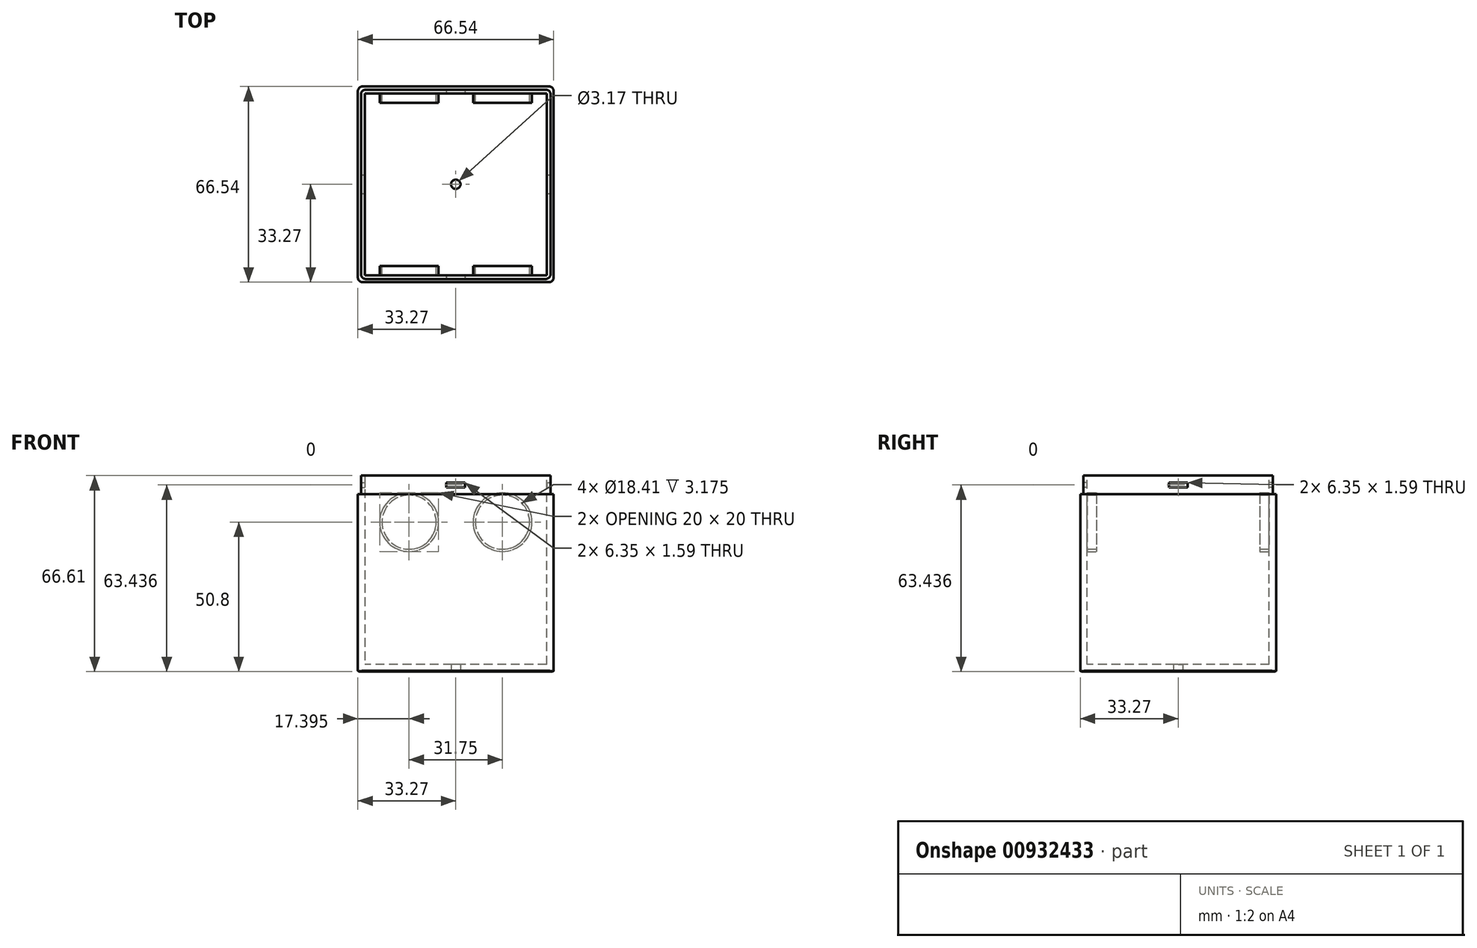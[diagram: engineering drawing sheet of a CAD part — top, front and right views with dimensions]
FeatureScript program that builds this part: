
annotation { "Feature Type Name" : "Feature", "Feature Type Description" : "" }
export const myFeature = defineFeature(function(context is Context, id is Id, definition is map)
    precondition{}
    {
        {
            var Q0;
            Q0=qCreatedBy(makeId("Top.planeOp"),FACE);
            var sketch = newSketch(context, id + "F0", { "sketchPlane" : qUnion([Q0])});
            skLineSegment(sketch, "E0.bottom", {"start": v(34.1, 34.1) * mm, "end": v(-34.1, 34.1) * mm});
            skLineSegment(sketch, "E0.top", {"start": v(34.1, -34.1) * mm, "end": v(-34.1, -34.1) * mm});
            skLineSegment(sketch, "E0.left", {"start": v(34.1, 34.1) * mm, "end": v(34.1, -34.1) * mm});
            skLineSegment(sketch, "E0.right", {"start": v(-34.1, 34.1) * mm, "end": v(-34.1, -34.1) * mm});
            skPoint(sketch, "E0.middle", {"position": v(0, 0) * mm});
            skSolve(sketch);
        }
        {
            var Q0;
            Q0 = qSketchRegion(id + "F0", true);
            extrude(context, id + "F1", {"entities" : qUnion([Q0]), "depth" : 66.61 * mm, "offsetDistance" : 25.4 * mm});
        }
        {
            var Q0;
            Q0=makeQuery(id+"F1.opExtrude","SWEPT_EDGE",EDGE,{"disambiguationData":[OSD([sQuery(id+"F0.wireOp",EDGE,"E0.bottom"),sQuery(id+"F0.wireOp",EDGE,"E0.right")])]});
            var Q1;
            Q1=makeQuery(id+"F1.opExtrude","CAP_EDGE",EDGE,{"disambiguationData":[OSD([sQuery(id+"F0.wireOp",EDGE,"E0.right")])],"isStart":true});
            var Q2;
            Q2=makeQuery(id+"F1.opExtrude","SWEPT_EDGE",EDGE,{"disambiguationData":[OSD([sQuery(id+"F0.wireOp",EDGE,"E0.top"),sQuery(id+"F0.wireOp",EDGE,"E0.right")])]});
            var Q3;
            Q3=makeQuery(id+"F1.opExtrude","SWEPT_EDGE",EDGE,{"disambiguationData":[OSD([sQuery(id+"F0.wireOp",EDGE,"E0.top"),sQuery(id+"F0.wireOp",EDGE,"E0.left")])]});
            var Q4;
            Q4=makeQuery(id+"F1.opExtrude","CAP_EDGE",EDGE,{"disambiguationData":[OSD([sQuery(id+"F0.wireOp",EDGE,"E0.top")])],"isStart":true});
            var Q5;
            Q5=makeQuery(id+"F1.opExtrude","CAP_FACE",FACE,{"disambiguationData":[OSD([sQuery(id+"F0.wireOp",EDGE,"E0.bottom"),sQuery(id+"F0.wireOp",EDGE,"E0.top"),sQuery(id+"F0.wireOp",EDGE,"E0.left"),sQuery(id+"F0.wireOp",EDGE,"E0.right")])],"isStart":true});
            var Q6;
            Q6=makeQuery(id+"F1.opExtrude","SWEPT_EDGE",EDGE,{"disambiguationData":[OSD([sQuery(id+"F0.wireOp",EDGE,"E0.bottom"),sQuery(id+"F0.wireOp",EDGE,"E0.left")])]});
            fillet(context, id + "F2", {"entities" : qUnion([Q0, Q1, Q2, Q3, Q4, Q5, Q6]), "radius" : 1.59 * mm, "tangentPropagation" : true, "allowEdgeOverflow" : false});
        }
        {
            var Q0;
            Q0=makeQuery(id+"F1.opExtrude","CAP_FACE",FACE,{"disambiguationData":[OSD([sQuery(id+"F0.wireOp",EDGE,"E0.bottom"),sQuery(id+"F0.wireOp",EDGE,"E0.top"),sQuery(id+"F0.wireOp",EDGE,"E0.left"),sQuery(id+"F0.wireOp",EDGE,"E0.right")])],"isStart":false});
            shell(context, id + "F3", {"entities" : qUnion([Q0]), "thickness" : 3.17 * mm});
        }
        {
            var Q0;
            Q0=makeQuery(id+"F3.opShell","OFFSET_FACE",FACE,{"disambiguationData":[OSD([sQuery(id+"F0.wireOp",EDGE,"E0.bottom"),sQuery(id+"F0.wireOp",EDGE,"E0.top"),sQuery(id+"F0.wireOp",EDGE,"E0.left"),sQuery(id+"F0.wireOp",EDGE,"E0.right")])]});
            var sketch = newSketch(context, id + "F4", { "sketchPlane" : qUnion([Q0])});
            skLineSegment(sketch, "E1.bottom", {"start": v(-30.92, 30.92) * mm, "end": v(-27.75, 30.92) * mm});
            skLineSegment(sketch, "E1.top", {"start": v(-30.92, 27.75) * mm, "end": v(-27.75, 27.75) * mm});
            skLineSegment(sketch, "E1.left", {"start": v(-30.92, 30.92) * mm, "end": v(-30.92, 27.75) * mm});
            skLineSegment(sketch, "E1.right", {"start": v(-27.75, 30.92) * mm, "end": v(-27.75, 27.75) * mm});
            skLineSegment(sketch, "E2.bottom", {"start": v(30.92, 30.92) * mm, "end": v(27.75, 30.92) * mm});
            skLineSegment(sketch, "E2.top", {"start": v(30.92, 27.75) * mm, "end": v(27.75, 27.75) * mm});
            skLineSegment(sketch, "E2.left", {"start": v(30.92, 30.92) * mm, "end": v(30.92, 27.75) * mm});
            skLineSegment(sketch, "E2.right", {"start": v(27.75, 30.92) * mm, "end": v(27.75, 27.75) * mm});
            skLineSegment(sketch, "E3.bottom", {"start": v(-30.92, -30.92) * mm, "end": v(-27.75, -30.92) * mm});
            skLineSegment(sketch, "E3.top", {"start": v(-30.92, -27.75) * mm, "end": v(-27.75, -27.75) * mm});
            skLineSegment(sketch, "E3.left", {"start": v(-30.92, -30.92) * mm, "end": v(-30.92, -27.75) * mm});
            skLineSegment(sketch, "E3.right", {"start": v(-27.75, -30.92) * mm, "end": v(-27.75, -27.75) * mm});
            skLineSegment(sketch, "E4.bottom", {"start": v(30.92, -30.92) * mm, "end": v(27.75, -30.92) * mm});
            skLineSegment(sketch, "E4.top", {"start": v(30.92, -27.75) * mm, "end": v(27.75, -27.75) * mm});
            skLineSegment(sketch, "E4.left", {"start": v(30.92, -30.92) * mm, "end": v(30.92, -27.75) * mm});
            skLineSegment(sketch, "E4.right", {"start": v(27.75, -30.92) * mm, "end": v(27.75, -27.75) * mm});
            skLineSegment(sketch, "E5.bottom", {"start": v(-3.18, 30.92) * mm, "end": v(3.17, 30.92) * mm});
            skLineSegment(sketch, "E5.top", {"start": v(-3.18, 27.75) * mm, "end": v(3.17, 27.75) * mm});
            skLineSegment(sketch, "E5.left", {"start": v(-3.18, 30.92) * mm, "end": v(-3.18, 27.75) * mm});
            skLineSegment(sketch, "E5.right", {"start": v(3.17, 30.92) * mm, "end": v(3.17, 27.75) * mm});
            skLineSegment(sketch, "E6.bottom", {"start": v(-30.92, 3.17) * mm, "end": v(-27.75, 3.17) * mm});
            skLineSegment(sketch, "E6.top", {"start": v(-30.92, -3.18) * mm, "end": v(-27.75, -3.18) * mm});
            skLineSegment(sketch, "E6.left", {"start": v(-30.92, 3.18) * mm, "end": v(-30.92, -3.18) * mm});
            skLineSegment(sketch, "E6.right", {"start": v(-27.75, 3.18) * mm, "end": v(-27.75, -3.18) * mm});
            skLineSegment(sketch, "E7.bottom", {"start": v(30.92, 3.18) * mm, "end": v(27.75, 3.18) * mm});
            skLineSegment(sketch, "E7.top", {"start": v(30.92, -3.17) * mm, "end": v(27.75, -3.17) * mm});
            skLineSegment(sketch, "E7.left", {"start": v(30.92, 3.18) * mm, "end": v(30.92, -3.17) * mm});
            skLineSegment(sketch, "E7.right", {"start": v(27.75, 3.18) * mm, "end": v(27.75, -3.17) * mm});
            skLineSegment(sketch, "E8.bottom", {"start": v(-3.17, -30.92) * mm, "end": v(3.18, -30.92) * mm});
            skLineSegment(sketch, "E8.top", {"start": v(-3.17, -27.75) * mm, "end": v(3.18, -27.75) * mm});
            skLineSegment(sketch, "E8.left", {"start": v(-3.17, -30.92) * mm, "end": v(-3.17, -27.75) * mm});
            skLineSegment(sketch, "E8.right", {"start": v(3.18, -30.92) * mm, "end": v(3.18, -27.75) * mm});
            skSolve(sketch);
        }
        {
            var Q0;
            Q0 = qSketchRegion(id + "F4", true);
            extrude(context, id + "F5", {"entities" : qUnion([Q0]), "operationType" : NewBodyOperationType.REMOVE, "depth" : 25.4 * mm, "offsetDistance" : 25.4 * mm});
        }
        {
            var Q0;
            Q0=makeQuery(id+"F1.opExtrude","CAP_FACE",FACE,{"disambiguationData":[OSD([sQuery(id+"F0.wireOp",EDGE,"E0.bottom"),sQuery(id+"F0.wireOp",EDGE,"E0.top"),sQuery(id+"F0.wireOp",EDGE,"E0.left"),sQuery(id+"F0.wireOp",EDGE,"E0.right")])],"isStart":true});
            var sketch = newSketch(context, id + "F6", { "sketchPlane" : qUnion([Q0])});
            skPoint(sketch, "E9.middle", {"position": v(0, 0) * mm});
            skCircle(sketch, "E10", {"center": v(0, 0) * mm, "radius": 1.59 * mm});
            skSolve(sketch);
        }
        {
            var Q0;
            Q0 = qSketchRegion(id + "F6", true);
            extrude(context, id + "F7", {"entities" : qUnion([Q0]), "operationType" : NewBodyOperationType.REMOVE, "oppositeDirection" : true, "depth" : 6.35 * mm, "offsetDistance" : 25.4 * mm});
        }
        {
            var Q0;
            Q0=makeQuery(id+"F1.opExtrude","CAP_FACE",FACE,{"disambiguationData":[OSD([sQuery(id+"F0.wireOp",EDGE,"E0.bottom"),sQuery(id+"F0.wireOp",EDGE,"E0.top"),sQuery(id+"F0.wireOp",EDGE,"E0.left"),sQuery(id+"F0.wireOp",EDGE,"E0.right")])],"isStart":false});
            var sketch = newSketch(context, id + "F8", { "sketchPlane" : qUnion([Q0])});
            skLineSegment(sketch, "E11.bottom", {"start": v(37.1, 37.9) * mm, "end": v(-37.1, 37.9) * mm});
            skLineSegment(sketch, "E11.top", {"start": v(37.1, -37.9) * mm, "end": v(-37.1, -37.9) * mm});
            skLineSegment(sketch, "E11.left", {"start": v(37.1, 37.9) * mm, "end": v(37.1, -37.9) * mm});
            skLineSegment(sketch, "E11.right", {"start": v(-37.1, 37.9) * mm, "end": v(-37.1, -37.9) * mm});
            skPoint(sketch, "E11.middle", {"position": v(0, 0) * mm});
            skLineSegment(sketch, "E12.bottom", {"start": v(30.6, 32.2) * mm, "end": v(-30.6, 32.2) * mm});
            skLineSegment(sketch, "E12.top", {"start": v(30.6, -32.2) * mm, "end": v(-30.6, -32.2) * mm});
            skLineSegment(sketch, "E12.left", {"start": v(32.2, 30.6) * mm, "end": v(32.2, -30.6) * mm});
            skLineSegment(sketch, "E12.right", {"start": v(-32.2, 30.6) * mm, "end": v(-32.2, -30.6) * mm});
            skPoint(sketch, "E13.visualSharp", {"position": v(32.2, 32.2) * mm});
            skArc(sketch, "E13.filletArc", {"start": v(32.2, 30.6) * mm, "mid": v(31.73, 31.73) * mm, "end": v(30.6, 32.2) * mm});
            skPoint(sketch, "E14.visualSharp", {"position": v(-32.2, 32.2) * mm});
            skArc(sketch, "E14.filletArc", {"start": v(-30.6, 32.2) * mm, "mid": v(-31.73, 31.73) * mm, "end": v(-32.2, 30.6) * mm});
            skPoint(sketch, "E15.visualSharp", {"position": v(-32.2, -32.2) * mm});
            skArc(sketch, "E15.filletArc", {"start": v(-32.2, -30.6) * mm, "mid": v(-31.73, -31.73) * mm, "end": v(-30.6, -32.2) * mm});
            skPoint(sketch, "E16.visualSharp", {"position": v(32.2, -32.2) * mm});
            skArc(sketch, "E16.filletArc", {"start": v(30.6, -32.2) * mm, "mid": v(31.73, -31.73) * mm, "end": v(32.2, -30.6) * mm});
            skSolve(sketch);
        }
        {
            var Q0;
            Q0 = qSketchRegion(id + "F8", true);
            extrude(context, id + "F9", {"entities" : qUnion([Q0]), "operationType" : NewBodyOperationType.REMOVE, "oppositeDirection" : true, "depth" : 6.35 * mm, "offsetDistance" : 25.4 * mm});
        }
        {
            var Q0;
            Q0=makeQuery(id+"F9.boolean.opBoolean","COPY",FACE,{"derivedFrom":makeQuery(id+"F9.opExtrude","SWEPT_FACE",FACE,{"disambiguationData":[OSD([sQuery(id+"F8.wireOp",EDGE,"E12.top")])]})});
            var sketch = newSketch(context, id + "F10", { "sketchPlane" : qUnion([Q0])});
            skLineSegment(sketch, "E17.bottom", {"start": v(3.17, 62.64) * mm, "end": v(-3.18, 62.64) * mm});
            skLineSegment(sketch, "E17.top", {"start": v(3.17, 64.23) * mm, "end": v(-3.18, 64.23) * mm});
            skLineSegment(sketch, "E17.left", {"start": v(3.17, 62.64) * mm, "end": v(3.17, 64.23) * mm});
            skLineSegment(sketch, "E17.right", {"start": v(-3.18, 62.64) * mm, "end": v(-3.18, 64.23) * mm});
            skPoint(sketch, "E17.middle", {"position": v(0, 63.44) * mm});
            skSolve(sketch);
        }
        {
            var Q0;
            Q0 = qSketchRegion(id + "F10", true);
            extrude(context, id + "F11", {"entities" : qUnion([Q0]), "operationType" : NewBodyOperationType.REMOVE, "endBound" : BoundingType.THROUGH_ALL, "oppositeDirection" : true, "depth" : 25.4 * mm, "offsetDistance" : 25.4 * mm});
        }
        {
            var Q0;
            Q0=makeQuery(id+"F9.boolean.opBoolean","COPY",FACE,{"derivedFrom":makeQuery(id+"F9.opExtrude","SWEPT_FACE",FACE,{"disambiguationData":[OSD([sQuery(id+"F8.wireOp",EDGE,"E12.left")])]})});
            var sketch = newSketch(context, id + "F12", { "sketchPlane" : qUnion([Q0])});
            skLineSegment(sketch, "E18.bottom", {"start": v(3.17, 64.23) * mm, "end": v(-3.18, 64.23) * mm});
            skLineSegment(sketch, "E18.top", {"start": v(3.17, 62.64) * mm, "end": v(-3.18, 62.64) * mm});
            skLineSegment(sketch, "E18.left", {"start": v(3.17, 64.23) * mm, "end": v(3.17, 62.64) * mm});
            skLineSegment(sketch, "E18.right", {"start": v(-3.18, 64.23) * mm, "end": v(-3.18, 62.64) * mm});
            skPoint(sketch, "E18.middle", {"position": v(0, 63.44) * mm});
            skSolve(sketch);
        }
        {
            var Q0;
            Q0 = qSketchRegion(id + "F12", true);
            extrude(context, id + "F13", {"entities" : qUnion([Q0]), "operationType" : NewBodyOperationType.REMOVE, "endBound" : BoundingType.THROUGH_ALL, "oppositeDirection" : true, "depth" : 25.4 * mm, "offsetDistance" : 25.4 * mm});
        }
        {
            var Q0;
            Q0=makeQuery(id+"F3.opShell","OFFSET_FACE",FACE,{"disambiguationData":[OSD([sQuery(id+"F0.wireOp",EDGE,"E0.bottom")])]});
            var sketch = newSketch(context, id + "F14", { "sketchPlane" : qUnion([Q0])});
            skCircle(sketch, "E19", {"center": v(-15.88, 50.8) * mm, "radius": 9.2 * mm});
            skCircle(sketch, "E20", {"center": v(15.88, 50.8) * mm, "radius": 9.2 * mm});
            skLineSegment(sketch, "E21", {"start": v(-15.88, 50.8) * mm, "end": v(15.88, 50.8) * mm, "construction": true});
            skLineSegment(sketch, "E22", {"start": v(0, 0) * mm, "end": v(0, 50.8) * mm, "construction": true});
            skCircle(sketch, "E23", {"center": v(-15.88, 50.8) * mm, "radius": 10 * mm});
            skCircle(sketch, "E24", {"center": v(15.88, 50.8) * mm, "radius": 10 * mm});
            skSolve(sketch);
        }
        {
            var Q0;
            Q0=makeQuery(id+"F14.imprint","IMPRINT",FACE,{"disambiguationData":[TD([[makeQuery(id+"F14.imprint","IMPRINT",EDGE,{"derivedFrom":sQuery(id+"F14.wireOp",EDGE,"E19")}),-1.0]])]});
            var Q1;
            Q1=makeQuery(id+"F14.imprint","IMPRINT",FACE,{"disambiguationData":[TD([[makeQuery(id+"F14.imprint","IMPRINT",EDGE,{"derivedFrom":sQuery(id+"F14.wireOp",EDGE,"E20")}),-1.0]])]});
            extrude(context, id + "F15", {"entities" : qUnion([Q0, Q1]), "operationType" : NewBodyOperationType.ADD, "endBound" : BoundingType.UP_TO_NEXT, "depth" : 25.4 * mm, "offsetDistance" : 25.4 * mm});
        }
        {
            var Q0;
            Q0=makeQuery(id+"F1.opExtrude","CAP_FACE",FACE,{"disambiguationData":[OSD([sQuery(id+"F0.wireOp",EDGE,"E0.bottom"),sQuery(id+"F0.wireOp",EDGE,"E0.top"),sQuery(id+"F0.wireOp",EDGE,"E0.left"),sQuery(id+"F0.wireOp",EDGE,"E0.right")])],"isStart":false});
            var sketch = newSketch(context, id + "F16", { "sketchPlane" : qUnion([Q0])});
            skLineSegment(sketch, "E25.bottom", {"start": v(27.75, 27.75) * mm, "end": v(-27.75, 27.75) * mm});
            skLineSegment(sketch, "E25.top", {"start": v(27.75, -27.75) * mm, "end": v(-27.75, -27.75) * mm});
            skLineSegment(sketch, "E25.left", {"start": v(27.75, 27.75) * mm, "end": v(27.75, -27.75) * mm});
            skLineSegment(sketch, "E25.right", {"start": v(-27.75, 27.75) * mm, "end": v(-27.75, -27.75) * mm});
            skPoint(sketch, "E25.middle", {"position": v(0, 0) * mm});
            skSolve(sketch);
        }
        {
            var Q0;
            Q0 = qSketchRegion(id + "F16", true);
            extrude(context, id + "F17", {"entities" : qUnion([Q0]), "operationType" : NewBodyOperationType.REMOVE, "oppositeDirection" : true, "depth" : 38.1 * mm, "offsetDistance" : 25.4 * mm});
        }
        {
            var Q0;
            Q0=makeQuery(id+"F3.opShell","OFFSET_FACE",FACE,{"disambiguationData":[OSD([sQuery(id+"F0.wireOp",EDGE,"E0.bottom"),sQuery(id+"F0.wireOp",EDGE,"E0.top"),sQuery(id+"F0.wireOp",EDGE,"E0.left"),sQuery(id+"F0.wireOp",EDGE,"E0.right")])]});
            var sketch = newSketch(context, id + "F18", { "sketchPlane" : qUnion([Q0])});
            skLineSegment(sketch, "E26.bottom", {"start": v(30.92, 30.92) * mm, "end": v(-30.92, 30.92) * mm});
            skLineSegment(sketch, "E26.top", {"start": v(30.92, -30.92) * mm, "end": v(-30.92, -30.92) * mm});
            skLineSegment(sketch, "E26.left", {"start": v(30.92, 30.92) * mm, "end": v(30.92, -30.92) * mm});
            skLineSegment(sketch, "E26.right", {"start": v(-30.92, 30.92) * mm, "end": v(-30.92, -30.92) * mm});
            skPoint(sketch, "E26.middle", {"position": v(0, 0) * mm});
            skSolve(sketch);
        }
        {
            var Q0;
            Q0 = qSketchRegion(id + "F18", true);
            extrude(context, id + "F19", {"entities" : qUnion([Q0]), "operationType" : NewBodyOperationType.REMOVE, "oppositeDirection" : true, "depth" : 0.8 * mm, "offsetDistance" : 25.4 * mm});
        }
        {
            var Q0;
            Q0=makeQuery(id+"F1.opExtrude","CAP_FACE",FACE,{"disambiguationData":[OSD([sQuery(id+"F0.wireOp",EDGE,"E0.bottom"),sQuery(id+"F0.wireOp",EDGE,"E0.top"),sQuery(id+"F0.wireOp",EDGE,"E0.left"),sQuery(id+"F0.wireOp",EDGE,"E0.right")])],"isStart":false});
            var sketch = newSketch(context, id + "F20", { "sketchPlane" : qUnion([Q0])});
            skLineSegment(sketch, "E27.bottom", {"start": v(34.1, 34.1) * mm, "end": v(-34.1, 34.1) * mm});
            skLineSegment(sketch, "E27.top", {"start": v(34.1, -34.1) * mm, "end": v(-34.1, -34.1) * mm});
            skLineSegment(sketch, "E27.left", {"start": v(34.1, 34.1) * mm, "end": v(34.1, -34.1) * mm});
            skLineSegment(sketch, "E27.right", {"start": v(-34.1, 34.1) * mm, "end": v(-34.1, -34.1) * mm});
            skPoint(sketch, "E27.middle", {"position": v(0, 0) * mm});
            skLineSegment(sketch, "E28.bottom", {"start": v(31.69, 33.27) * mm, "end": v(-31.69, 33.27) * mm});
            skLineSegment(sketch, "E28.top", {"start": v(31.69, -33.27) * mm, "end": v(-31.69, -33.27) * mm});
            skLineSegment(sketch, "E28.left", {"start": v(33.27, 31.69) * mm, "end": v(33.27, -31.69) * mm});
            skLineSegment(sketch, "E28.right", {"start": v(-33.27, 31.69) * mm, "end": v(-33.27, -31.69) * mm});
            skPoint(sketch, "E29.visualSharp", {"position": v(33.27, 33.27) * mm});
            skArc(sketch, "E29.filletArc", {"start": v(33.27, 31.69) * mm, "mid": v(32.8, 32.8) * mm, "end": v(31.69, 33.27) * mm});
            skPoint(sketch, "E30.visualSharp", {"position": v(-33.27, 33.27) * mm});
            skArc(sketch, "E30.filletArc", {"start": v(-31.69, 33.27) * mm, "mid": v(-32.8, 32.8) * mm, "end": v(-33.27, 31.69) * mm});
            skPoint(sketch, "E31.visualSharp", {"position": v(-33.27, -33.27) * mm});
            skArc(sketch, "E31.filletArc", {"start": v(-33.27, -31.69) * mm, "mid": v(-32.8, -32.8) * mm, "end": v(-31.69, -33.27) * mm});
            skPoint(sketch, "E32.visualSharp", {"position": v(33.27, -33.27) * mm});
            skArc(sketch, "E32.filletArc", {"start": v(31.69, -33.27) * mm, "mid": v(32.8, -32.8) * mm, "end": v(33.27, -31.69) * mm});
            skSolve(sketch);
        }
        {
            var Q0;
            Q0=makeQuery(id+"F20.imprint","IMPRINT",FACE,{"disambiguationData":[TD([[makeQuery(id+"F20.imprint","IMPRINT",EDGE,{"derivedFrom":sQuery(id+"F20.wireOp",EDGE,"E27.bottom")}),1.0]])]});
            extrude(context, id + "F21", {"entities" : qUnion([Q0]), "operationType" : NewBodyOperationType.REMOVE, "endBound" : BoundingType.THROUGH_ALL, "oppositeDirection" : true, "depth" : 25.4 * mm, "offsetDistance" : 25.4 * mm});
        }
    });
